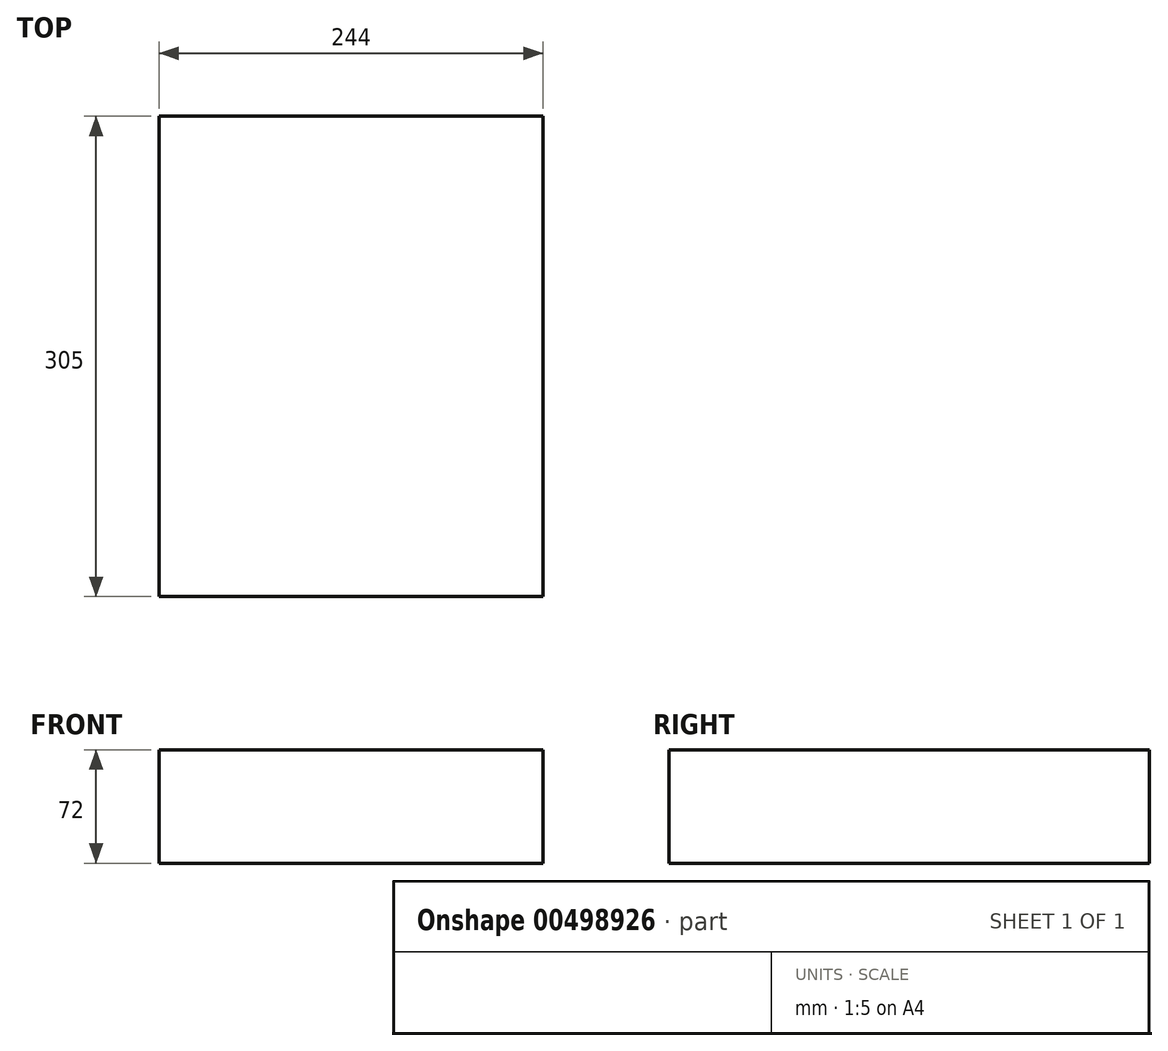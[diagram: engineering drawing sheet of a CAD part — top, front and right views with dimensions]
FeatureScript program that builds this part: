
annotation { "Feature Type Name" : "Feature", "Feature Type Description" : "" }
export const myFeature = defineFeature(function(context is Context, id is Id, definition is map)
    precondition{}
    {
        {
            var Q0;
            Q0=qCreatedBy(makeId("Top.planeOp"),FACE);
            var sketch = newSketch(context, id + "F0", { "sketchPlane" : qUnion([Q0])});
            skLineSegment(sketch, "E0.bottom", {"start": v(122, 152.5) * mm, "end": v(-122, 152.5) * mm});
            skLineSegment(sketch, "E0.top", {"start": v(122, -152.5) * mm, "end": v(-122, -152.5) * mm});
            skLineSegment(sketch, "E0.left", {"start": v(122, 152.5) * mm, "end": v(122, -152.5) * mm});
            skLineSegment(sketch, "E0.right", {"start": v(-122, 152.5) * mm, "end": v(-122, -152.5) * mm});
            skPoint(sketch, "E0.middle", {"position": v(0, 0) * mm});
            skSolve(sketch);
        }
        {
            var Q0;
            Q0=makeQuery(id+"F0.imprint","IMPRINT",FACE,{"disambiguationData":[TD([[makeQuery(id+"F0.imprint","IMPRINT",EDGE,{"derivedFrom":sQuery(id+"F0.wireOp",EDGE,"E0.bottom")}),1.0]])]});
            extrude(context, id + "F1", {"entities" : qUnion([Q0]), "depth" : 72 * mm, "offsetDistance" : 25 * mm});
        }
    });
